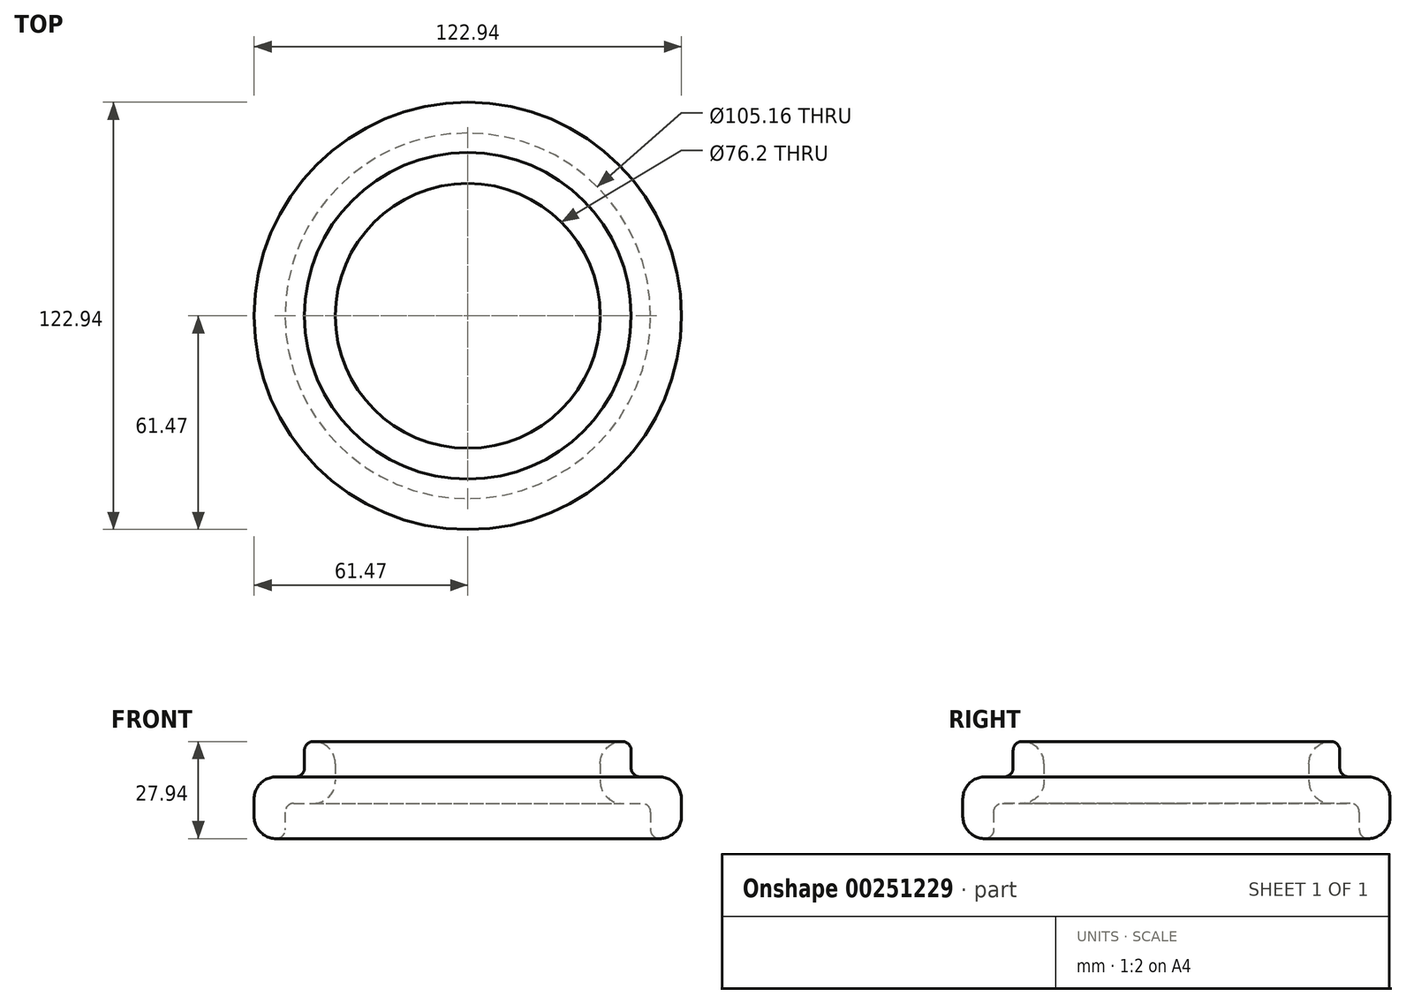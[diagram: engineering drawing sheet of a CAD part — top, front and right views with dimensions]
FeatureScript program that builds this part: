
annotation { "Feature Type Name" : "Feature", "Feature Type Description" : "" }
export const myFeature = defineFeature(function(context is Context, id is Id, definition is map)
    precondition{}
    {
        {
            var Q0;
            Q0=qCreatedBy(makeId("Front.planeOp"),FACE);
            var sketch = newSketch(context, id + "F0", { "sketchPlane" : qUnion([Q0])});
            skLineSegment(sketch, "E0.bottom", {"start": v(-55.12, 7.62) * mm, "end": v(-49.53, 7.62) * mm});
            skLineSegment(sketch, "E0.top", {"start": v(-55.12, -10.16) * mm, "end": v(-55.12, -10.16) * mm});
            skLineSegment(sketch, "E0.left", {"start": v(-61.47, 1.27) * mm, "end": v(-61.47, -3.81) * mm});
            skLineSegment(sketch, "E0.right", {"start": v(-52.58, -2.54) * mm, "end": v(-52.58, -7.62) * mm});
            skLineSegment(sketch, "E1.bottom", {"start": v(-44.45, 17.78) * mm, "end": v(-44.45, 17.78) * mm});
            skLineSegment(sketch, "E1.top", {"start": v(-50.04, 0) * mm, "end": v(-44.45, 0) * mm});
            skLineSegment(sketch, "E1.left", {"start": v(-47, 15.24) * mm, "end": v(-47, 10.16) * mm});
            skLineSegment(sketch, "E1.right", {"start": v(-38.1, 11.43) * mm, "end": v(-38.1, 6.35) * mm});
            skPoint(sketch, "E2", {"position": v(-52.58, 0) * mm});
            skPoint(sketch, "E3.visualSharp", {"position": v(-61.47, 7.62) * mm});
            skArc(sketch, "E3.filletArc", {"start": v(-55.12, 7.62) * mm, "mid": v(-59.6, 5.76) * mm, "end": v(-61.47, 1.27) * mm});
            skPoint(sketch, "E4.visualSharp", {"position": v(-38.1, 17.78) * mm});
            skArc(sketch, "E4.filletArc", {"start": v(-38.1, 11.43) * mm, "mid": v(-39.96, 15.92) * mm, "end": v(-44.45, 17.78) * mm});
            skPoint(sketch, "E5.visualSharp", {"position": v(-47, 17.78) * mm});
            skArc(sketch, "E5.filletArc", {"start": v(-44.45, 17.78) * mm, "mid": v(-46.25, 17.04) * mm, "end": v(-47, 15.24) * mm});
            skPoint(sketch, "E6.visualSharp", {"position": v(-61.47, -10.16) * mm});
            skArc(sketch, "E6.filletArc", {"start": v(-61.47, -3.81) * mm, "mid": v(-59.6, -8.3) * mm, "end": v(-55.12, -10.16) * mm});
            skPoint(sketch, "E7.visualSharp", {"position": v(-52.58, -10.16) * mm});
            skArc(sketch, "E7.filletArc", {"start": v(-55.12, -10.16) * mm, "mid": v(-53.32, -9.42) * mm, "end": v(-52.58, -7.62) * mm});
            skPoint(sketch, "E8.visualSharp", {"position": v(-38.1, 0) * mm});
            skArc(sketch, "E8.filletArc", {"start": v(-44.45, 0) * mm, "mid": v(-39.96, 1.86) * mm, "end": v(-38.1, 6.35) * mm});
            skPoint(sketch, "E9.visualSharp", {"position": v(-47, 7.62) * mm});
            skArc(sketch, "E9.filletArc", {"start": v(-49.53, 7.62) * mm, "mid": v(-47.73, 8.36) * mm, "end": v(-47, 10.16) * mm});
            skArc(sketch, "E10.filletArc", {"start": v(-50.04, 0) * mm, "mid": v(-51.83, -0.74) * mm, "end": v(-52.58, -2.54) * mm});
            skLineSegment(sketch, "E11", {"start": v(0, 0) * mm, "end": v(0, 26.47) * mm, "construction": true});
            skSolve(sketch);
        }
        {
            var Q0;
            Q0=makeQuery(id+"F0.imprint","IMPRINT",FACE,{"disambiguationData":[TD([[makeQuery(id+"F0.imprint","IMPRINT",EDGE,{"derivedFrom":sQuery(id+"F0.wireOp",EDGE,"E0.bottom")}),-1.0]])]});
            var Q1;
            Q1=sQuery(id+"F0.wireOp",EDGE,"E11");
            revolve(context, id + "F1", {"entities" : qUnion([Q0]), "axis" : qUnion([Q1]), "revolveType" : RevolveType.FULL});
        }
    });
